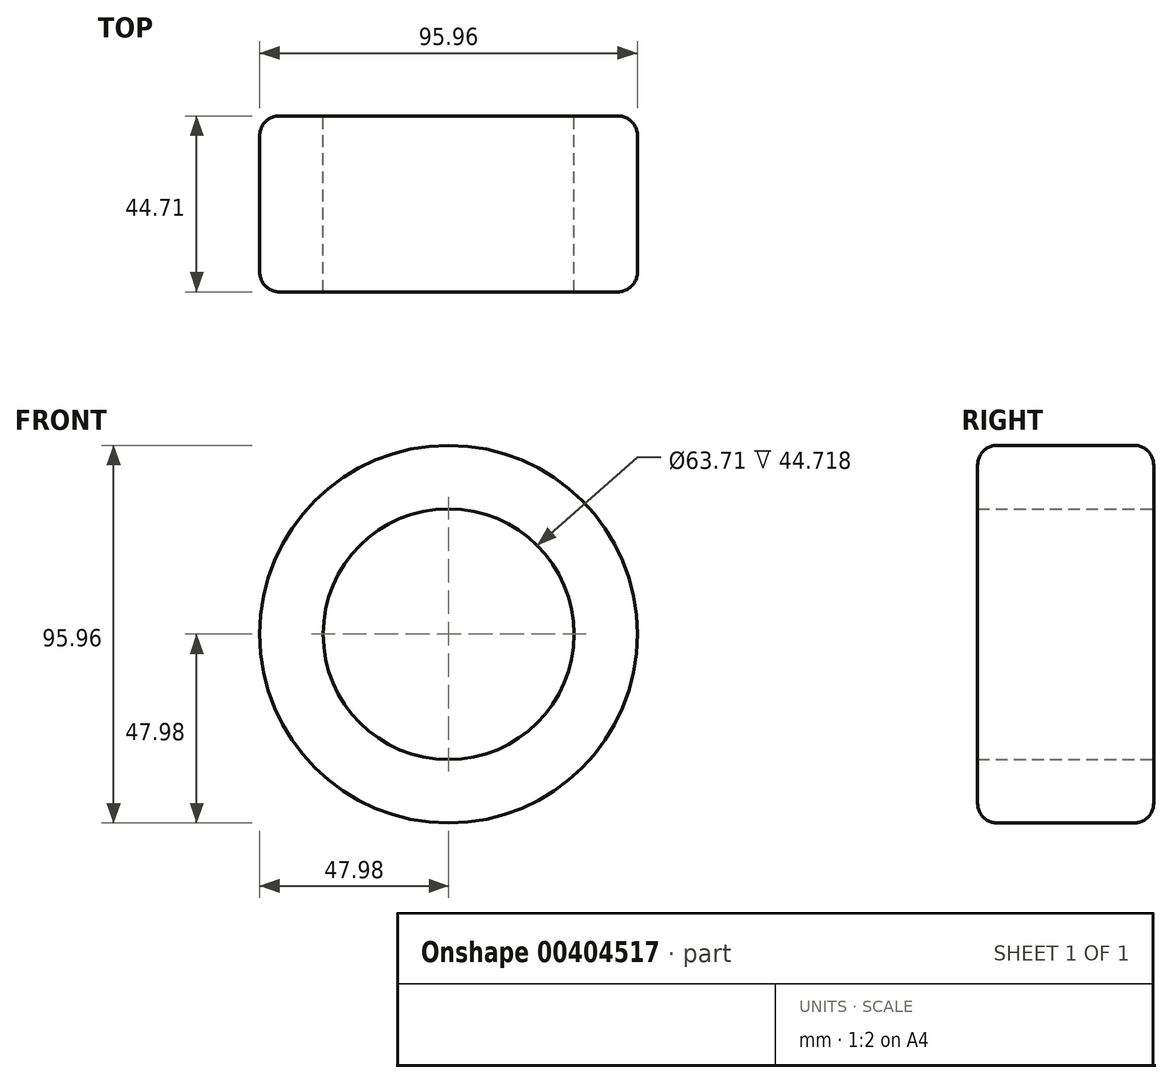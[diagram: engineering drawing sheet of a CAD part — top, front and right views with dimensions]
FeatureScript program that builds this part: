
annotation { "Feature Type Name" : "Feature", "Feature Type Description" : "" }
export const myFeature = defineFeature(function(context is Context, id is Id, definition is map)
    precondition{}
    {
        {
            var Q0;
            Q0=qCreatedBy(makeId("Right.planeOp"),FACE);
            var sketch = newSketch(context, id + "F0", { "sketchPlane" : qUnion([Q0])});
            skLineSegment(sketch, "E0.bottom", {"start": v(-23.07, 47.98) * mm, "end": v(21.64, 47.98) * mm});
            skLineSegment(sketch, "E0.top", {"start": v(-23.07, 31.85) * mm, "end": v(21.64, 31.85) * mm});
            skLineSegment(sketch, "E0.left", {"start": v(-23.07, 47.98) * mm, "end": v(-23.07, 31.85) * mm});
            skLineSegment(sketch, "E0.right", {"start": v(21.64, 47.98) * mm, "end": v(21.64, 31.85) * mm});
            skSolve(sketch);
        }
        {
            var Q0;
            Q0=qCreatedBy(makeId("Right.planeOp"),FACE);
            var sketch = newSketch(context, id + "F1", { "sketchPlane" : qUnion([Q0])});
            skLineSegment(sketch, "E1", {"start": v(-54.52, 0) * mm, "end": v(62.16, 0) * mm});
            skSolve(sketch);
        }
        {
            var Q0;
            Q0=makeQuery(id+"F0.imprint","IMPRINT",FACE,{"disambiguationData":[TD([[makeQuery(id+"F0.imprint","IMPRINT",EDGE,{"derivedFrom":sQuery(id+"F0.wireOp",EDGE,"E0.bottom")}),-1.0]])]});
            var Q1;
            Q1=sQuery(id+"F0.wireOp",EDGE,"E0.bottom");
            var Q2;
            Q2=sQuery(id+"F0.wireOp",EDGE,"E0.top");
            var Q3;
            Q3=sQuery(id+"F0.wireOp",EDGE,"E0.left");
            var Q4;
            Q4=sQuery(id+"F0.wireOp",EDGE,"E0.right");
            var Q5;
            Q5=sQuery(id+"F1.wireOp",EDGE,"E1");
            revolve(context, id + "F2", {"bodyType" : ToolBodyType.SURFACE, "entities" : qUnion([Q0]), "surfaceEntities" : qUnion([Q1, Q2, Q3, Q4]), "axis" : qUnion([Q5]), "revolveType" : RevolveType.FULL});
        }
        {
            var Q0;
            Q0=makeQuery(id+"F2.opRevolve","SWEPT_EDGE",EDGE,{"disambiguationData":[OSD([sQuery(id+"F0.wireOp",VERTEX,"E0.left.start")])]});
            var Q1;
            Q1=makeQuery(id+"F2.opRevolve","SWEPT_EDGE",EDGE,{"disambiguationData":[OSD([sQuery(id+"F0.wireOp",VERTEX,"E0.right.start")])]});
            fillet(context, id + "F3", {"entities" : qUnion([Q0, Q1]), "radius" : 5 * mm, "tangentPropagation" : true, "allowEdgeOverflow" : false});
        }
    });
